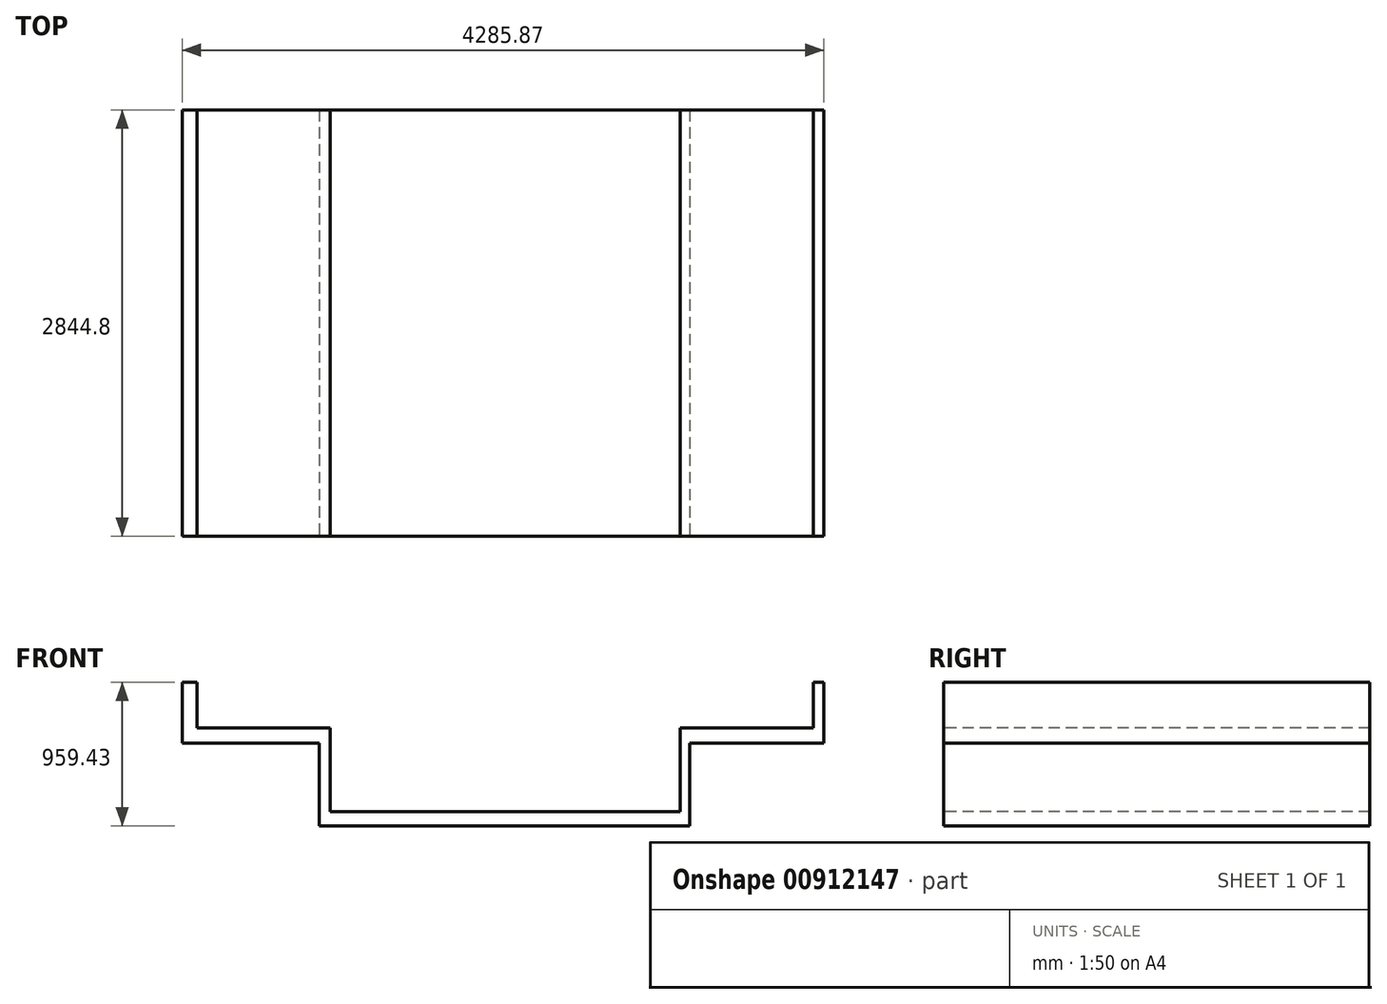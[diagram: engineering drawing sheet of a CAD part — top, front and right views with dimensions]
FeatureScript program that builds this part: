
annotation { "Feature Type Name" : "Feature", "Feature Type Description" : "" }
export const myFeature = defineFeature(function(context is Context, id is Id, definition is map)
    precondition{}
    {
        {
            var Q0;
            Q0=qCreatedBy(makeId("Front.planeOp"),FACE);
            var sketch = newSketch(context, id + "F0", { "sketchPlane" : qUnion([Q0])});
            skLineSegment(sketch, "E0", {"start": v(113.62, -63.8) * mm, "end": v(2450.42, -63.8) * mm});
            skLineSegment(sketch, "E1", {"start": v(2450.42, -63.8) * mm, "end": v(2450.42, 495) * mm});
            skLineSegment(sketch, "E2", {"start": v(2450.42, 495) * mm, "end": v(3339.42, 495) * mm});
            skLineSegment(sketch, "E3", {"start": v(3339.42, 495) * mm, "end": v(3339.42, 799.8) * mm});
            skLineSegment(sketch, "E4", {"start": v(113.62, -63.8) * mm, "end": v(113.62, 495) * mm});
            skLineSegment(sketch, "E5", {"start": v(113.62, 495) * mm, "end": v(-775.38, 495) * mm});
            skLineSegment(sketch, "E6", {"start": v(-775.38, 495) * mm, "end": v(-775.38, 799.8) * mm});
            skLineSegment(sketch, "E7", {"start": v(-775.38, 799.8) * mm, "end": v(-873.81, 799.8) * mm});
            skLineSegment(sketch, "E8", {"start": v(-873.81, 799.8) * mm, "end": v(-873.81, 392.9) * mm});
            skLineSegment(sketch, "E9", {"start": v(-873.81, 392.9) * mm, "end": v(42.76, 392.9) * mm});
            skLineSegment(sketch, "E10", {"start": v(42.76, 392.9) * mm, "end": v(42.76, -159.63) * mm});
            skLineSegment(sketch, "E11", {"start": v(42.76, -159.63) * mm, "end": v(2515.97, -159.63) * mm});
            skLineSegment(sketch, "E12", {"start": v(2515.97, -159.63) * mm, "end": v(2515.97, 392.9) * mm});
            skLineSegment(sketch, "E13", {"start": v(2515.97, 392.9) * mm, "end": v(3412.06, 392.9) * mm});
            skLineSegment(sketch, "E14", {"start": v(3412.06, 392.9) * mm, "end": v(3412.06, 799.8) * mm});
            skLineSegment(sketch, "E15", {"start": v(3412.06, 799.8) * mm, "end": v(3339.42, 799.8) * mm});
            skSolve(sketch);
        }
        {
            var Q0;
            Q0=makeQuery(id+"F0.imprint","IMPRINT",FACE,{"disambiguationData":[TD([[makeQuery(id+"F0.imprint","IMPRINT",EDGE,{"derivedFrom":sQuery(id+"F0.wireOp",EDGE,"E0")}),-1.0]])]});
            extrude(context, id + "F1", {"entities" : qUnion([Q0]), "oppositeDirection" : true, "depth" : 2844.8 * mm, "offsetDistance" : 25.4 * mm});
        }
    });
